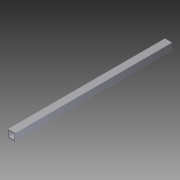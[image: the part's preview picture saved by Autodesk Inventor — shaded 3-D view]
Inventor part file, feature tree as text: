
AUTODESK INVENTOR PART (.ipt)
format: ipt  version: 2012 (Build 160160000, 160)  size: 74,752 bytes
history: native  units: in
note: dims shown in document units (in); Inventor stores cm internally (conversion verified against a paired STEP export)
features: extrude x1, sketch x1
ambient origin geometry x8: Origin, YZ Plane, XZ Plane, XY Plane, X Axis, Y Axis, Z Axis, Center Point
bodies: Solid1 (feature_tree)
feature tree (2):
  extrude  "Extrusion1"  Depth=1.0in
  sketch  "Sketch1"  dims[d0=1.0in d1=1.0in d2=0.125in d3=0.125in d4=0.125in d5=0.125in d6=21.75in d7=0.0in]
